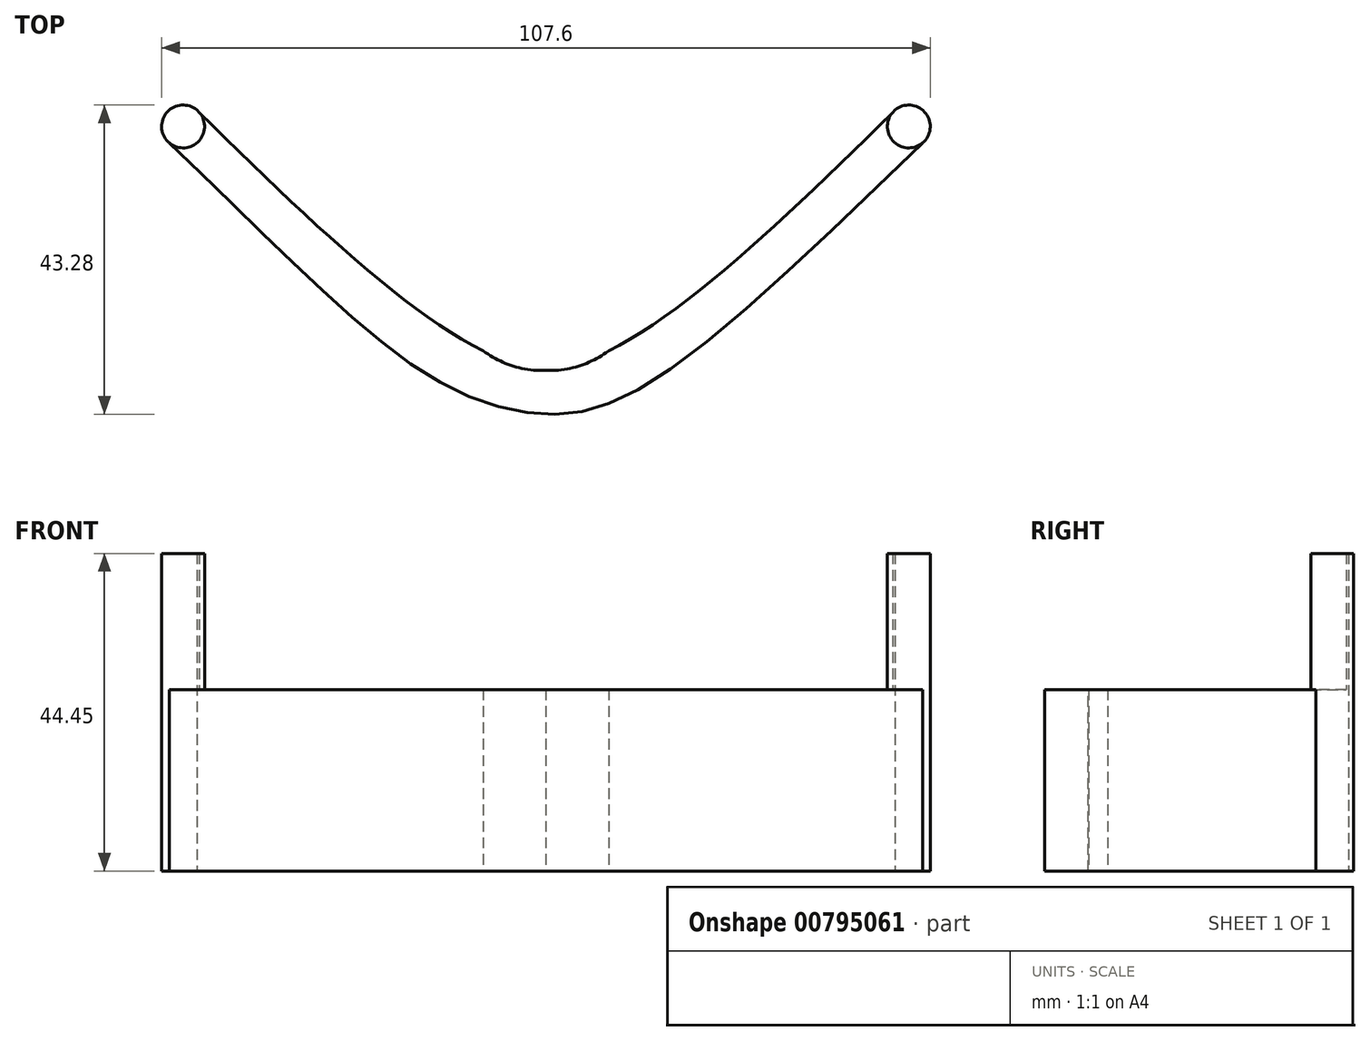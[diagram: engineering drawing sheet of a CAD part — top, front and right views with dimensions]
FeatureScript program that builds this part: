
annotation { "Feature Type Name" : "Feature", "Feature Type Description" : "" }
export const myFeature = defineFeature(function(context is Context, id is Id, definition is map)
    precondition{}
    {
        {
            var Q0;
            Q0=qCreatedBy(makeId("Top.planeOp"),FACE);
            var sketch = newSketch(context, id + "F0", { "sketchPlane" : qUnion([Q0])});
            skPoint(sketch, "E0", {"position": v(-475.84, 73.92) * mm});
            skCircle(sketch, "E1", {"center": v(-475.84, 73.92) * mm, "radius": 3.65 * mm});
            skLineSegment(sketch, "E2", {"start": v(-475.84, 73.92) * mm, "end": v(-473.27, 76.52) * mm});
            skLineSegment(sketch, "E3", {"start": v(-473.27, 76.52) * mm, "end": v(-478.4, 71.32) * mm});
            skLineSegment(sketch, "E4", {"start": v(-20.8, 335.07) * mm, "end": v(-20.8, 237.1) * mm});
            skFitSpline(sketch, "E5", {"points": [v(-69.68, -325.42) * mm, v(-20.34, -361.86) * mm, v(-6.04, -353.32) * mm, v(0, -344.62) * mm], "startDerivative": vector(106.85, -105.44) * mm, "endDerivative": vector(23.99, 38.44) * mm});
            skFitSpline(sketch, "E6.MirrorCS", {"points": [v(28.07, -325.42) * mm, v(-21.27, -361.86) * mm, v(-35.56, -353.32) * mm, v(-41.6, -344.62) * mm], "startDerivative": vector(-106.85, -105.44) * mm, "endDerivative": vector(-23.99, 38.44) * mm});
            skPoint(sketch, "E7", {"position": v(-20.8, -361.84) * mm});
            skFitSpline(sketch, "E8", {"points": [v(-73.53, -330.03) * mm, v(-51.9, -350.85) * mm, v(-33.93, -364.46) * mm, v(-19.77, -368) * mm, v(-5.89, -363.37) * mm, v(31.92, -330.03) * mm], "startDerivative": vector(101.84, -97.17) * mm, "endDerivative": vector(147.39, 142.73) * mm});
            skLineSegment(sketch, "E9", {"start": v(31.92, -330.03) * mm, "end": v(28.07, -325.42) * mm});
            skLineSegment(sketch, "E10", {"start": v(-69.68, -325.42) * mm, "end": v(-73.53, -330.03) * mm});
            skPoint(sketch, "E11", {"position": v(30, -327.72) * mm});
            skPoint(sketch, "E12", {"position": v(-71.6, -327.72) * mm});
            skCircle(sketch, "E13", {"center": v(30, -327.72) * mm, "radius": 3 * mm});
            skCircle(sketch, "E14", {"center": v(-71.6, -327.72) * mm, "radius": 3 * mm});
            skSolve(sketch);
        }
        {
            var Q0;
            {var subQ8=sQuery(id+"F0.wireOp",EDGE,"E8");Q0=makeQuery(id+"F0.imprint","IMPRINT",FACE,{"disambiguationData":[TD([[makeQuery(id+"F0.imprint","IMPRINT",EDGE,{"derivedFrom":subQ8}),1.0]])]});}
            extrude(context, id + "F1", {"entities" : qUnion([Q0]), "depth" : 25.4 * mm, "offsetDistance" : 25.4 * mm});
        }
        {
            var Q0;
            {var subQ0=sQuery(id+"F0.wireOp",EDGE,"E9");Q0=makeQuery(id+"F0.imprint","IMPRINT",FACE,{"disambiguationData":[TD([[makeQuery(id+"F0.imprint","IMPRINT",EDGE,{"derivedFrom":subQ0}),-1.0]])]});}
            var Q1;
            {var subQ1=sQuery(id+"F0.wireOp",EDGE,"E9");Q1=makeQuery(id+"F0.imprint","IMPRINT",FACE,{"disambiguationData":[TD([[makeQuery(id+"F0.imprint","IMPRINT",EDGE,{"derivedFrom":subQ1}),1.0]])]});}
            var Q2;
            {var subQ1=sQuery(id+"F0.wireOp",EDGE,"E10");Q2=makeQuery(id+"F0.imprint","IMPRINT",FACE,{"disambiguationData":[TD([[makeQuery(id+"F0.imprint","IMPRINT",EDGE,{"derivedFrom":subQ1}),1.0]])]});}
            var Q3;
            {var subQ0=sQuery(id+"F0.wireOp",EDGE,"E10");Q3=makeQuery(id+"F0.imprint","IMPRINT",FACE,{"disambiguationData":[TD([[makeQuery(id+"F0.imprint","IMPRINT",EDGE,{"derivedFrom":subQ0}),-1.0]])]});}
            extrude(context, id + "F2", {"entities" : qUnion([Q0, Q1, Q2, Q3]), "operationType" : NewBodyOperationType.ADD, "depth" : 44.45 * mm, "offsetDistance" : 25.4 * mm});
        }
    });
